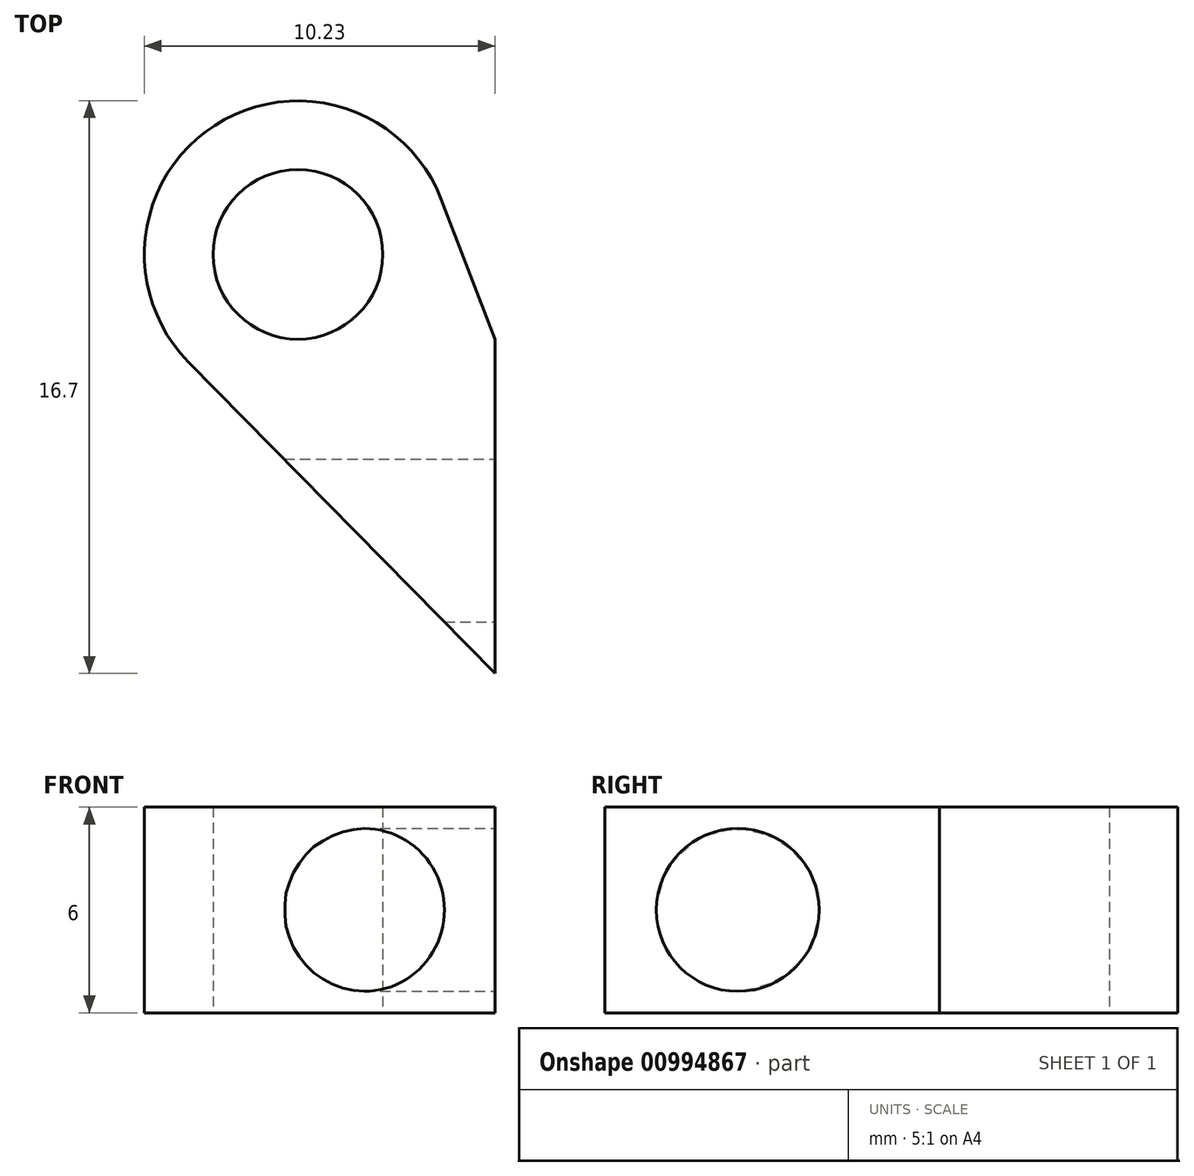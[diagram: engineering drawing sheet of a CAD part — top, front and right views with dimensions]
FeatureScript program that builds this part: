
annotation { "Feature Type Name" : "Feature", "Feature Type Description" : "" }
export const myFeature = defineFeature(function(context is Context, id is Id, definition is map)
    precondition{}
    {
        {
            var Q0;
            Q0=qCreatedBy(makeId("Top.planeOp"),FACE);
            var sketch = newSketch(context, id + "F0", { "sketchPlane" : qUnion([Q0])});
            skCircle(sketch, "E0", {"center": v(-15.25, 0.21) * mm, "radius": 2.48 * mm});
            skLineSegment(sketch, "E1", {"start": v(15.25, 0.21) * mm, "end": v(-15.25, 0.21) * mm, "construction": true});
            skLineSegment(sketch, "E2", {"start": v(0, 0.21) * mm, "end": v(0, 0) * mm, "construction": true});
            skCircle(sketch, "E3", {"center": v(-15.25, 0.21) * mm, "radius": 4.47 * mm});
            skLineSegment(sketch, "E4", {"start": v(-10.78, 0.21) * mm, "end": v(-10.77, -10.72) * mm});
            skLineSegment(sketch, "E5", {"start": v(-15.25, -4.26) * mm, "end": v(-15.25, -9.01) * mm, "construction": true});
            skLineSegment(sketch, "E6", {"start": v(-15.25, -9.01) * mm, "end": v(-15.25, -11.01) * mm, "construction": true});
            skLineSegment(sketch, "E7", {"start": v(-15.25, -9.01) * mm, "end": v(-10.77, -9.01) * mm, "construction": true});
            skLineSegment(sketch, "E8", {"start": v(0, -9.01) * mm, "end": v(-9.5, -9.01) * mm, "construction": true});
            skLineSegment(sketch, "E9", {"start": v(-9.5, -9.01) * mm, "end": v(-12.45, -9.01) * mm});
            skLineSegment(sketch, "E10", {"start": v(-9.5, -9.01) * mm, "end": v(-9.5, -4.26) * mm});
            skLineSegment(sketch, "E11", {"start": v(-9.5, -4.26) * mm, "end": v(-10.78, -4.26) * mm});
            skLineSegment(sketch, "E12", {"start": v(-9.5, -4.26) * mm, "end": v(-9.5, -2.26) * mm});
            skLineSegment(sketch, "E13", {"start": v(-9.5, -9.01) * mm, "end": v(-9.5, -12.01) * mm});
            skPoint(sketch, "E14.orphan", {"position": v(-18.75, -11.01) * mm});
            skPoint(sketch, "E15.orphan", {"position": v(-10.77, -11.01) * mm});
            skLineSegment(sketch, "E16", {"start": v(-9.5, -2.26) * mm, "end": v(-11.07, 1.82) * mm});
            skLineSegment(sketch, "E17", {"start": v(-9.5, -12.01) * mm, "end": v(-18.44, -2.93) * mm});
            skLineSegment(sketch, "E18.trimOffspring", {"start": v(-12.45, -9.01) * mm, "end": v(0, -9.01) * mm, "construction": true});
            skLineSegment(sketch, "E19", {"start": v(-18.44, -2.93) * mm, "end": v(-21.08, -5.53) * mm});
            skLineSegment(sketch, "E20", {"start": v(-21.08, -5.53) * mm, "end": v(-12.14, -14.61) * mm});
            skLineSegment(sketch, "E21", {"start": v(-12.14, -14.61) * mm, "end": v(-9.5, -12.01) * mm});
            skSolve(sketch);
        }
        {
            var Q0;
            {var subQ0=sQuery(id+"F0.wireOp",EDGE,"E17");var subQ1=sQuery(id+"F0.wireOp",EDGE,"E4");var subQ2=makeQuery(id+"F0.imprint","INTERSECT",VERTEX,{"derivedFrom":[subQ1,subQ0]});Q0=makeQuery(id+"F0.imprint","IMPRINT",FACE,{"disambiguationData":[TD([[makeQuery(id+"F0.imprint","IMPRINT",EDGE,{"disambiguationData":[TD([[subQ2,1.0]])],"derivedFrom":subQ1}),-1.0]])]});}
            var Q1;
            Q1=makeQuery(id+"F0.imprint","IMPRINT",FACE,{"disambiguationData":[TD([[makeQuery(id+"F0.imprint","IMPRINT",EDGE,{"derivedFrom":sQuery(id+"F0.wireOp",EDGE,"E0")}),-1.0]])]});
            var Q2;
            {var subQ0=sQuery(id+"F0.wireOp",EDGE,"E11");Q2=makeQuery(id+"F0.imprint","IMPRINT",FACE,{"disambiguationData":[TD([[makeQuery(id+"F0.imprint","IMPRINT",EDGE,{"derivedFrom":subQ0}),-1.0]])]});}
            var Q3;
            {var subQ4=sQuery(id+"F0.wireOp",EDGE,"E10");Q3=makeQuery(id+"F0.imprint","IMPRINT",FACE,{"disambiguationData":[TD([[makeQuery(id+"F0.imprint","IMPRINT",EDGE,{"derivedFrom":subQ4}),1.0]])]});}
            var Q4;
            {var subQ5=sQuery(id+"F0.wireOp",EDGE,"E13");Q4=makeQuery(id+"F0.imprint","IMPRINT",FACE,{"disambiguationData":[TD([[makeQuery(id+"F0.imprint","IMPRINT",EDGE,{"derivedFrom":subQ5}),-1.0]])]});}
            var Q5;
            {var subQ0=sQuery(id+"F0.wireOp",EDGE,"E4");var subQ6=sQuery(id+"F0.wireOp",EDGE,"E3");var subQ8=makeQuery(id+"F0.imprint","INTERSECT",VERTEX,{"derivedFrom":[subQ6,subQ0]});Q5=makeQuery(id+"F0.imprint","IMPRINT",FACE,{"disambiguationData":[TD([[makeQuery(id+"F0.imprint","IMPRINT",EDGE,{"disambiguationData":[TD([[subQ8,-1.0]])],"derivedFrom":subQ0}),-1.0]])]});}
            extrude(context, id + "F1", {"entities" : qUnion([Q0, Q1, Q2, Q3, Q4, Q5]), "depth" : 6 * mm, "offsetDistance" : 25 * mm});
        }
        {
            var Q0;
            Q0=makeQuery(id+"F1.opExtrude","SWEPT_FACE",FACE,{"disambiguationData":[OSD([sQuery(id+"F0.wireOp",EDGE,"E10"),sQuery(id+"F0.wireOp",EDGE,"E12"),sQuery(id+"F0.wireOp",EDGE,"E13")])]});
            var sketch = newSketch(context, id + "F2", { "sketchPlane" : qUnion([Q0])});
            skLineSegment(sketch, "E22", {"start": v(-12.01, 3) * mm, "end": v(-10.51, 3) * mm});
            skLineSegment(sketch, "E23", {"start": v(-10.51, 3) * mm, "end": v(-2.26, 3) * mm, "construction": true});
            skCircle(sketch, "E24", {"center": v(-8.14, 3) * mm, "radius": 2.38 * mm});
            skCircle(sketch, "E25", {"center": v(-8.14, 3) * mm, "radius": 1 * mm});
            skSolve(sketch);
        }
        {
            var Q0;
            Q0=makeQuery(id+"F2.imprint","IMPRINT",FACE,{"disambiguationData":[TD([[makeQuery(id+"F2.imprint","IMPRINT",EDGE,{"derivedFrom":sQuery(id+"F2.wireOp",EDGE,"E25")}),1.0]])]});
            var Q1;
            Q1=makeQuery(id+"F2.imprint","IMPRINT",FACE,{"disambiguationData":[TD([[makeQuery(id+"F2.imprint","IMPRINT",EDGE,{"derivedFrom":sQuery(id+"F2.wireOp",EDGE,"E24")}),1.0]])]});
            extrude(context, id + "F3", {"entities" : qUnion([Q0, Q1]), "operationType" : NewBodyOperationType.REMOVE, "endBound" : BoundingType.UP_TO_NEXT, "oppositeDirection" : true, "depth" : 25 * mm, "offsetDistance" : 25 * mm});
        }
        {
            var Q0;
            Q0=makeQuery(id+"F1.opExtrude","SWEPT_FACE",FACE,{"disambiguationData":[OSD([sQuery(id+"F0.wireOp",EDGE,"E10"),sQuery(id+"F0.wireOp",EDGE,"E12"),sQuery(id+"F0.wireOp",EDGE,"E13")])]});
            var sketch = newSketch(context, id + "F4", { "sketchPlane" : qUnion([Q0])});
            skLineSegment(sketch, "E26", {"start": v(-12.01, 3) * mm, "end": v(-10.51, 3) * mm, "construction": true});
            skLineSegment(sketch, "E27", {"start": v(-12.01, 3) * mm, "end": v(-2.26, 3) * mm, "construction": true});
            skCircle(sketch, "E28", {"center": v(-8.14, 3) * mm, "radius": 2.38 * mm, "construction": true});
            skCircle(sketch, "E29", {"center": v(-8.14, 3) * mm, "radius": 1 * mm});
            skSolve(sketch);
        }
        {
            var Q0;
            Q0 = qSketchRegion(id + "F4", true);
            var Q1;
            Q1=makeQuery(id+"F4.imprint","IMPRINT",FACE,{"disambiguationData":[TD([[makeQuery(id+"F4.imprint","IMPRINT",EDGE,{"derivedFrom":makeQuery(id+"F3.boolean.opBoolean","COPY",EDGE,{"derivedFrom":makeQuery(id+"F3.opExtrude","CAP_EDGE",EDGE,{"disambiguationData":[OSD([sQuery(id+"F2.wireOp",EDGE,"E24")])],"isStart":true})})}),1.0]])]});
            extrude(context, id + "F5", {"entities" : qUnion([Q0, Q1]), "operationType" : NewBodyOperationType.ADD, "oppositeDirection" : true, "depth" : 2 * mm, "offsetDistance" : 25 * mm});
        }
        {
            var Q0;
            Q0 = qSketchRegion(id + "F4", true);
            extrude(context, id + "F6", {"entities" : qUnion([Q0]), "operationType" : NewBodyOperationType.REMOVE, "endBound" : BoundingType.UP_TO_NEXT, "oppositeDirection" : true, "depth" : 25 * mm, "offsetDistance" : 25 * mm});
        }
        {
            var Q0;
            {var subQ0=sQuery(id+"F0.wireOp",EDGE,"E19");Q0=makeQuery(id+"F0.imprint","IMPRINT",FACE,{"disambiguationData":[TD([[makeQuery(id+"F0.imprint","IMPRINT",EDGE,{"derivedFrom":subQ0}),1.0]])]});}
            extrude(context, id + "F7", {"entities" : qUnion([Q0]), "operationType" : NewBodyOperationType.REMOVE, "depth" : 25 * mm, "offsetDistance" : 25 * mm});
        }
    });
